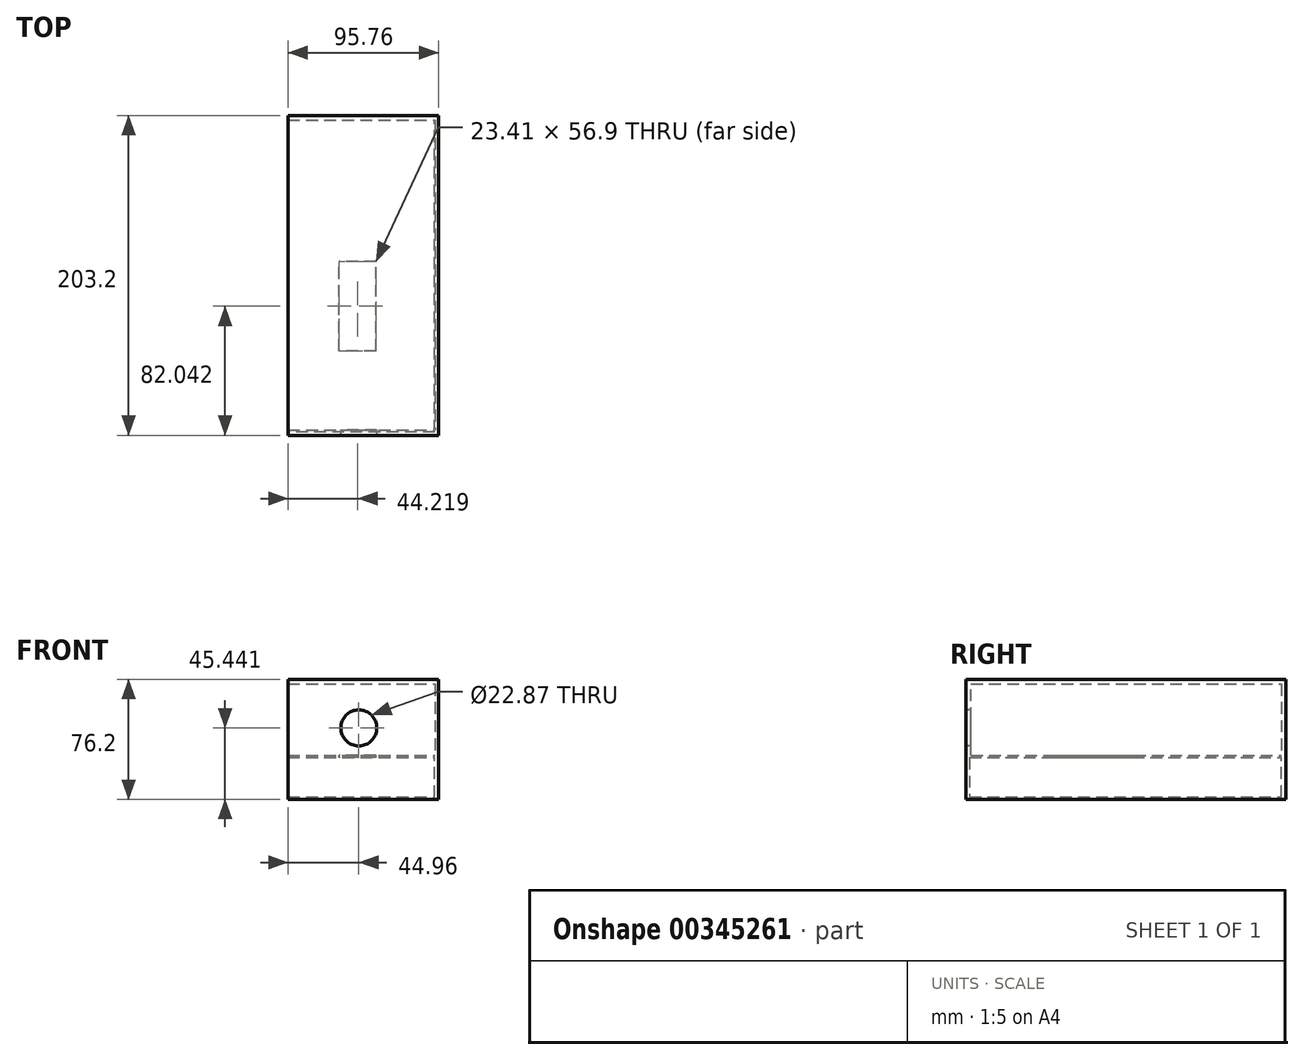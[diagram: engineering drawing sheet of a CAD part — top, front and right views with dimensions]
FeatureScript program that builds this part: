
annotation { "Feature Type Name" : "Feature", "Feature Type Description" : "" }
export const myFeature = defineFeature(function(context is Context, id is Id, definition is map)
    precondition{}
    {
        {
            var Q0;
            Q0=qCreatedBy(makeId("Top.planeOp"),FACE);
            var sketch = newSketch(context, id + "F0", { "sketchPlane" : qUnion([Q0])});
            skLineSegment(sketch, "E0.bottom", {"start": v(50.8, 101.6) * mm, "end": v(-50.8, 101.6) * mm});
            skLineSegment(sketch, "E0.top", {"start": v(50.8, -101.6) * mm, "end": v(-50.8, -101.6) * mm});
            skLineSegment(sketch, "E0.left", {"start": v(50.8, 101.6) * mm, "end": v(50.8, -101.6) * mm});
            skLineSegment(sketch, "E0.right", {"start": v(-50.8, 101.6) * mm, "end": v(-50.8, -101.6) * mm});
            skPoint(sketch, "E0.middle", {"position": v(0, 0) * mm});
            skSolve(sketch);
        }
        {
            var Q0;
            Q0 = qSketchRegion(id + "F0", true);
            extrude(context, id + "F1", {"entities" : qUnion([Q0]), "depth" : 76.2 * mm});
        }
        {
            var Q0;
            Q0=makeQuery(id+"F1.opExtrude","SWEPT_FACE",FACE,{"disambiguationData":[OSD([sQuery(id+"F0.wireOp",EDGE,"E0.top")])]});
            var sketch = newSketch(context, id + "F2", { "sketchPlane" : qUnion([Q0])});
            skLineSegment(sketch, "E1.bottom", {"start": v(-48.08, 73.26) * mm, "end": v(48.36, 73.26) * mm});
            skLineSegment(sketch, "E1.top", {"start": v(-48.08, 2.69) * mm, "end": v(48.36, 2.69) * mm});
            skLineSegment(sketch, "E1.left", {"start": v(-48.08, 73.26) * mm, "end": v(-48.08, 2.69) * mm});
            skLineSegment(sketch, "E1.right", {"start": v(48.36, 73.26) * mm, "end": v(48.36, 2.69) * mm});
            skSolve(sketch);
        }
        {
            var Q0;
            Q0 = qSketchRegion(id + "F2", true);
            extrude(context, id + "F3", {"entities" : qUnion([Q0]), "operationType" : NewBodyOperationType.REMOVE, "oppositeDirection" : true, "depth" : 258.57 * mm});
        }
        {
            var Q0;
            Q0=makeQuery(id+"F1.opExtrude","SWEPT_FACE",FACE,{"disambiguationData":[OSD([sQuery(id+"F0.wireOp",EDGE,"E0.top")])]});
            var sketch = newSketch(context, id + "F4", { "sketchPlane" : qUnion([Q0])});
            skLineSegment(sketch, "E2.bottom", {"start": v(-50.8, 76.2) * mm, "end": v(50.8, 76.2) * mm});
            skLineSegment(sketch, "E2.top", {"start": v(-50.8, 0) * mm, "end": v(50.8, 0) * mm});
            skLineSegment(sketch, "E2.left", {"start": v(-50.8, 76.2) * mm, "end": v(-50.8, 0) * mm});
            skLineSegment(sketch, "E2.right", {"start": v(50.8, 76.2) * mm, "end": v(50.8, 0) * mm});
            skSolve(sketch);
        }
        {
            var Q0;
            Q0 = qSketchRegion(id + "F4", true);
            extrude(context, id + "F5", {"entities" : qUnion([Q0]), "operationType" : NewBodyOperationType.ADD, "oppositeDirection" : true, "depth" : 3.3 * mm});
        }
        {
            var Q0;
            Q0=makeQuery(id+"F5.boolean.opBoolean","MERGE",FACE,{"derivedFrom":[makeQuery(id+"F1.opExtrude","SWEPT_FACE",FACE,{"disambiguationData":[OSD([sQuery(id+"F0.wireOp",EDGE,"E0.top")])]}),makeQuery(id+"F5.opExtrude","CAP_FACE",FACE,{"disambiguationData":[OSD([sQuery(id+"F4.wireOp",EDGE,"E2.bottom"),sQuery(id+"F4.wireOp",EDGE,"E2.top"),sQuery(id+"F4.wireOp",EDGE,"E2.left"),sQuery(id+"F4.wireOp",EDGE,"E2.right")])],"isStart":true})]});
            var sketch = newSketch(context, id + "F6", { "sketchPlane" : qUnion([Q0])});
            skCircle(sketch, "E3", {"center": v(0, 45.44) * mm, "radius": 11.43 * mm});
            skSolve(sketch);
        }
        {
            var Q0;
            Q0 = qSketchRegion(id + "F6", true);
            extrude(context, id + "F7", {"entities" : qUnion([Q0]), "operationType" : NewBodyOperationType.REMOVE, "oppositeDirection" : true, "depth" : 25.4 * mm});
        }
        {
            var Q0;
            Q0=makeQuery(id+"F1.opExtrude","SWEPT_FACE",FACE,{"disambiguationData":[OSD([sQuery(id+"F0.wireOp",EDGE,"E0.bottom")])]});
            var sketch = newSketch(context, id + "F8", { "sketchPlane" : qUnion([Q0])});
            skLineSegment(sketch, "E4.bottom", {"start": v(-50.8, 0) * mm, "end": v(49.74, 0) * mm});
            skLineSegment(sketch, "E4.top", {"start": v(-50.8, 27.99) * mm, "end": v(49.74, 27.99) * mm});
            skLineSegment(sketch, "E4.left", {"start": v(-50.8, 0) * mm, "end": v(-50.8, 27.99) * mm});
            skLineSegment(sketch, "E4.right", {"start": v(49.74, 0) * mm, "end": v(49.74, 27.99) * mm});
            skSolve(sketch);
        }
        {
            var Q0;
            Q0 = qSketchRegion(id + "F8", true);
            extrude(context, id + "F9", {"entities" : qUnion([Q0]), "operationType" : NewBodyOperationType.ADD, "oppositeDirection" : true, "depth" : 203.2 * mm});
        }
        {
            var Q0;
            Q0=makeQuery(id+"F9.boolean.opBoolean","MERGE",FACE,{"derivedFrom":[makeQuery(id+"F1.opExtrude","SWEPT_FACE",FACE,{"disambiguationData":[OSD([sQuery(id+"F0.wireOp",EDGE,"E0.bottom")])]}),makeQuery(id+"F9.opExtrude","CAP_FACE",FACE,{"disambiguationData":[OSD([sQuery(id+"F8.wireOp",EDGE,"E4.bottom"),sQuery(id+"F8.wireOp",EDGE,"E4.top"),sQuery(id+"F8.wireOp",EDGE,"E4.left"),sQuery(id+"F8.wireOp",EDGE,"E4.right")])],"isStart":true})]});
            var sketch = newSketch(context, id + "F10", { "sketchPlane" : qUnion([Q0])});
            skLineSegment(sketch, "E5.bottom", {"start": v(-48.23, 26.52) * mm, "end": v(47.83, 26.52) * mm});
            skLineSegment(sketch, "E5.top", {"start": v(-48.23, 1.54) * mm, "end": v(47.83, 1.54) * mm});
            skLineSegment(sketch, "E5.left", {"start": v(-48.23, 26.52) * mm, "end": v(-48.23, 1.54) * mm});
            skLineSegment(sketch, "E5.right", {"start": v(47.83, 26.52) * mm, "end": v(47.83, 1.54) * mm});
            skSolve(sketch);
        }
        {
            var Q0;
            Q0 = qSketchRegion(id + "F10", true);
            extrude(context, id + "F11", {"entities" : qUnion([Q0]), "operationType" : NewBodyOperationType.REMOVE, "oppositeDirection" : true, "depth" : 200.9 * mm});
        }
        {
            var Q0;
            Q0=makeQuery(id+"F9.opExtrude","SWEPT_FACE",FACE,{"disambiguationData":[OSD([sQuery(id+"F8.wireOp",EDGE,"E4.top")])]});
            var sketch = newSketch(context, id + "F12", { "sketchPlane" : qUnion([Q0])});
            skLineSegment(sketch, "E6.bottom", {"start": v(-12.45, 8.9) * mm, "end": v(10.96, 8.9) * mm});
            skLineSegment(sketch, "E6.top", {"start": v(-12.45, -48) * mm, "end": v(10.96, -48) * mm});
            skLineSegment(sketch, "E6.left", {"start": v(-12.45, 8.9) * mm, "end": v(-12.45, -48) * mm});
            skLineSegment(sketch, "E6.right", {"start": v(10.96, 8.9) * mm, "end": v(10.96, -48) * mm});
            skSolve(sketch);
        }
        {
            var Q0;
            Q0 = qSketchRegion(id + "F12", true);
            extrude(context, id + "F13", {"entities" : qUnion([Q0]), "operationType" : NewBodyOperationType.REMOVE, "oppositeDirection" : true, "depth" : 9.65 * mm, "hasSecondDirection" : true, "secondDirectionOppositeDirection" : false, "secondDirectionDepth" : 11.94 * mm});
        }
        {
            var Q0;
            Q0=makeQuery(id+"F1.opExtrude","SWEPT_FACE",FACE,{"disambiguationData":[OSD([sQuery(id+"F0.wireOp",EDGE,"E0.right")])]});
            var sketch = newSketch(context, id + "F14", { "sketchPlane" : qUnion([Q0])});
            skLineSegment(sketch, "E7.bottom", {"start": v(-109.85, 82.37) * mm, "end": v(123.35, 82.37) * mm});
            skLineSegment(sketch, "E7.top", {"start": v(-109.85, -18.03) * mm, "end": v(123.35, -18.03) * mm});
            skLineSegment(sketch, "E7.left", {"start": v(-109.85, 82.37) * mm, "end": v(-109.85, -18.03) * mm});
            skLineSegment(sketch, "E7.right", {"start": v(123.35, 82.37) * mm, "end": v(123.35, -18.03) * mm});
            skSolve(sketch);
        }
        {
            var Q0;
            Q0 = qSketchRegion(id + "F14", true);
            extrude(context, id + "F15", {"entities" : qUnion([Q0]), "operationType" : NewBodyOperationType.REMOVE, "oppositeDirection" : true, "depth" : 5.84 * mm});
        }
        {
            var Q0;
            Q0=makeQuery(id+"F9.boolean.opBoolean","MERGE",FACE,{"derivedFrom":[makeQuery(id+"F1.opExtrude","SWEPT_FACE",FACE,{"disambiguationData":[OSD([sQuery(id+"F0.wireOp",EDGE,"E0.bottom")])]}),makeQuery(id+"F9.opExtrude","CAP_FACE",FACE,{"disambiguationData":[OSD([sQuery(id+"F8.wireOp",EDGE,"E4.bottom"),sQuery(id+"F8.wireOp",EDGE,"E4.top"),sQuery(id+"F8.wireOp",EDGE,"E4.left"),sQuery(id+"F8.wireOp",EDGE,"E4.right")])],"isStart":true})]});
            var sketch = newSketch(context, id + "F16", { "sketchPlane" : qUnion([Q0])});
            skLineSegment(sketch, "E8.bottom", {"start": v(-50.8, 76.2) * mm, "end": v(44.96, 76.2) * mm});
            skLineSegment(sketch, "E8.top", {"start": v(-50.8, 0) * mm, "end": v(44.96, 0) * mm});
            skLineSegment(sketch, "E8.left", {"start": v(-50.8, 76.2) * mm, "end": v(-50.8, 0) * mm});
            skLineSegment(sketch, "E8.right", {"start": v(44.96, 76.2) * mm, "end": v(44.96, 0) * mm});
            skSolve(sketch);
        }
        {
            var Q0;
            Q0 = qSketchRegion(id + "F16", true);
            extrude(context, id + "F17", {"entities" : qUnion([Q0]), "operationType" : NewBodyOperationType.ADD, "oppositeDirection" : true, "depth" : 2.8 * mm});
        }
    });
